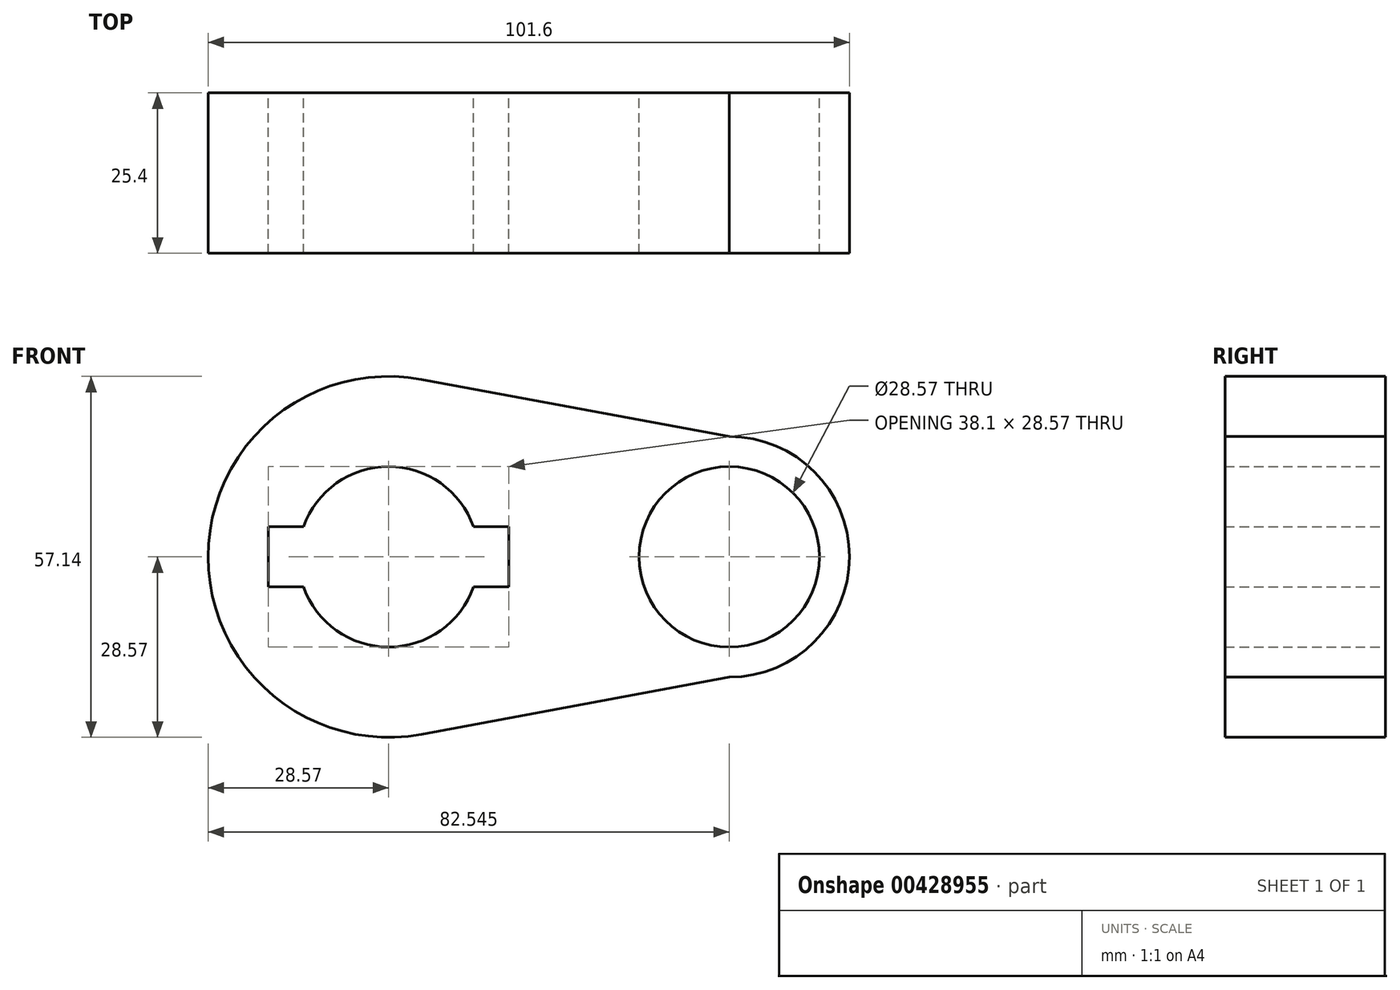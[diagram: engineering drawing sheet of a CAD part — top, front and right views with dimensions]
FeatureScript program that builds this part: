
annotation { "Feature Type Name" : "Feature", "Feature Type Description" : "" }
export const myFeature = defineFeature(function(context is Context, id is Id, definition is map)
    precondition{}
    {
        {
            var Q0;
            Q0=qCreatedBy(makeId("Front.planeOp"),FACE);
            var sketch = newSketch(context, id + "F0", { "sketchPlane" : qUnion([Q0])});
            skCircle(sketch, "E0", {"center": v(0, 0) * mm, "radius": 28.58 * mm});
            skCircle(sketch, "E1", {"center": v(53.98, 0) * mm, "radius": 19.05 * mm});
            skCircle(sketch, "E2", {"center": v(0, 0) * mm, "radius": 14.29 * mm});
            skCircle(sketch, "E3", {"center": v(53.98, 0) * mm, "radius": 14.29 * mm});
            skLineSegment(sketch, "E4.bottom", {"start": v(-19.05, 4.76) * mm, "end": v(19.05, 4.76) * mm});
            skLineSegment(sketch, "E4.top", {"start": v(-19.05, -4.76) * mm, "end": v(19.05, -4.76) * mm});
            skLineSegment(sketch, "E4.left", {"start": v(-19.05, 4.76) * mm, "end": v(-19.05, -4.76) * mm});
            skLineSegment(sketch, "E4.right", {"start": v(19.05, 4.76) * mm, "end": v(19.05, -4.76) * mm});
            skLineSegment(sketch, "E5", {"start": v(5.21, 28.1) * mm, "end": v(53.98, 19.05) * mm});
            skLineSegment(sketch, "E6", {"start": v(5.21, -28.1) * mm, "end": v(53.98, -19.05) * mm});
            skSolve(sketch);
        }
        {
            var Q0;
            Q0 = qSketchRegion(id + "F0", true);
            extrude(context, id + "F1", {"entities" : qUnion([Q0]), "depth" : 25.4 * mm});
        }
    });
